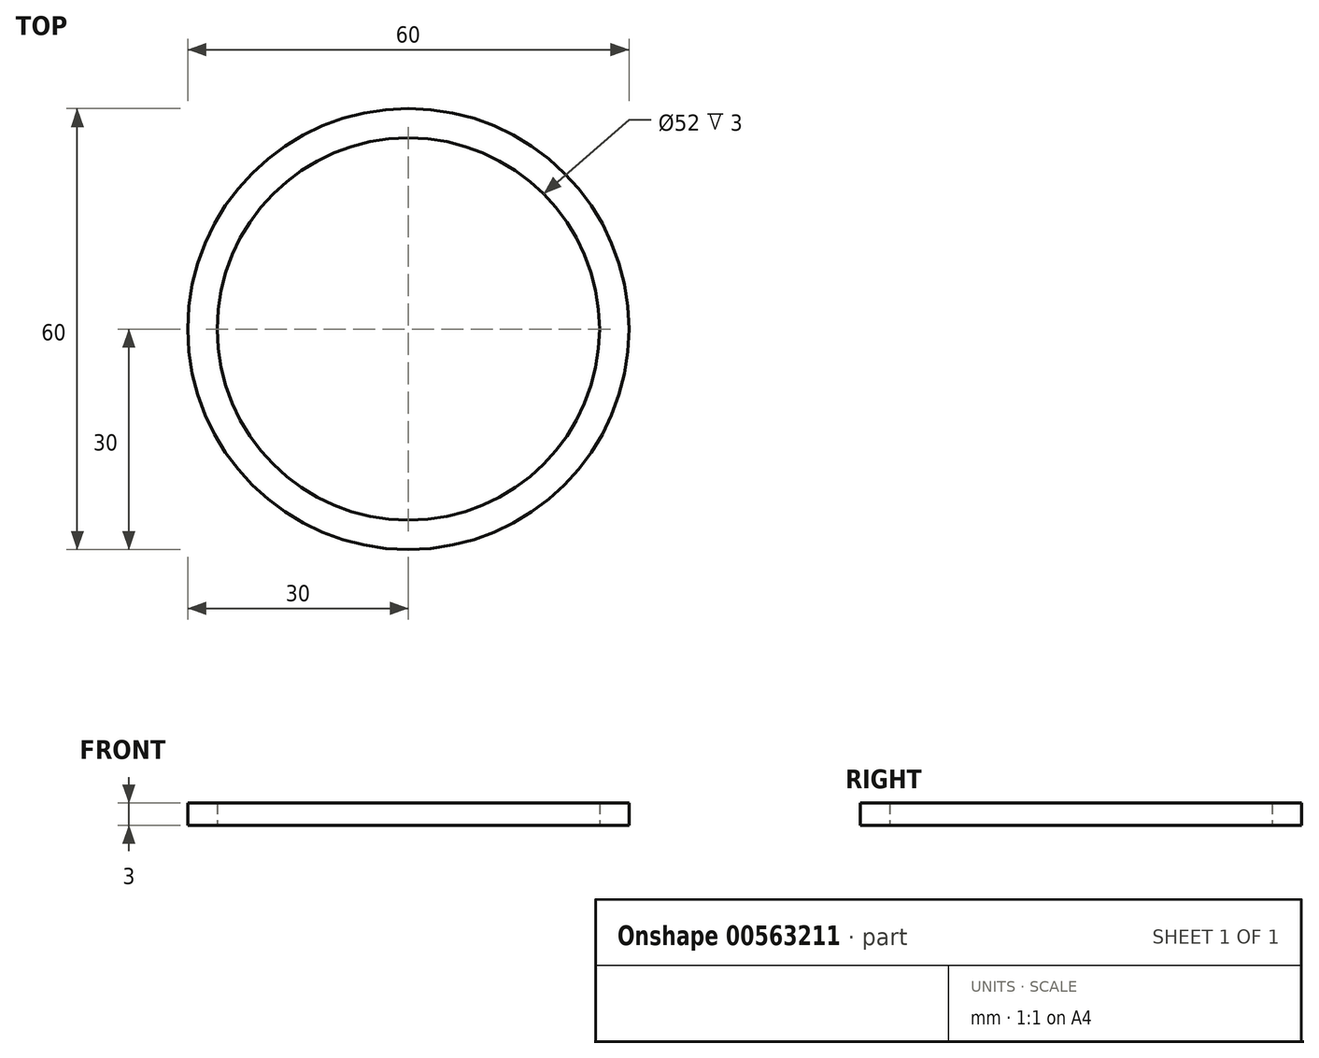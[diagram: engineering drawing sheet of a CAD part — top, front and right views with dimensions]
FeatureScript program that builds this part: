
annotation { "Feature Type Name" : "Feature", "Feature Type Description" : "" }
export const myFeature = defineFeature(function(context is Context, id is Id, definition is map)
    precondition{}
    {
        {
            var Q0;
            Q0=qCreatedBy(makeId("Top.planeOp"),FACE);
            var sketch = newSketch(context, id + "F0", { "sketchPlane" : qUnion([Q0])});
            skCircle(sketch, "E0", {"center": v(0, 0) * mm, "radius": 30 * mm});
            skCircle(sketch, "E1", {"center": v(0, 0) * mm, "radius": 26 * mm});
            skSolve(sketch);
        }
        {
            var Q0;
            Q0=qSketchRegion(id+"F0",true);
            extrude(context, id + "F1", {"entities" : qUnion([Q0]), "endBound" : BoundingType.SYMMETRIC, "depth" : 3 * mm, "offsetDistance" : 25 * mm});
        }
    });
